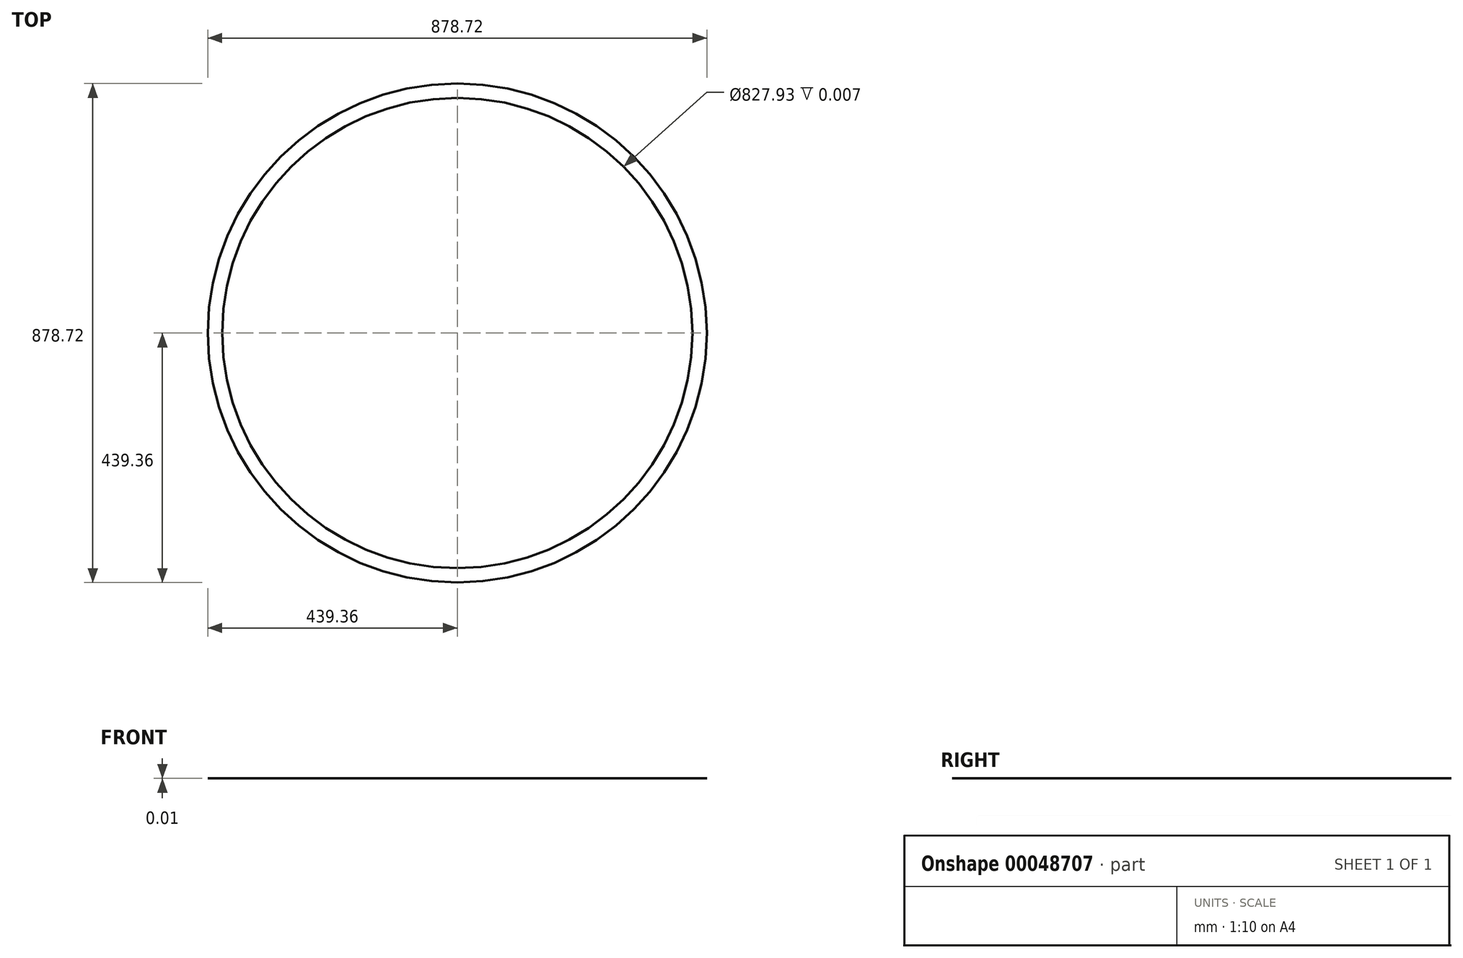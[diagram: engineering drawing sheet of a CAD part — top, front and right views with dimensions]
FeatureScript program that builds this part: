
annotation { "Feature Type Name" : "Feature", "Feature Type Description" : "" }
export const myFeature = defineFeature(function(context is Context, id is Id, definition is map)
    precondition{}
    {
        {
            var Q0;
            Q0=qCreatedBy(makeId("Top.planeOp"),FACE);
            var sketch = newSketch(context, id + "F0", { "sketchPlane" : qUnion([Q0])});
            skCircle(sketch, "E0", {"center": v(0, 0) * mm, "radius": 439.36 * mm});
            skCircle(sketch, "E1", {"center": v(0, 0) * mm, "radius": 413.96 * mm});
            skSolve(sketch);
        }
        {
            var Q0;
            Q0 = qSketchRegion(id + "F0", true);
            extrude(context, id + "F1", {"entities" : qUnion([Q0]), "depth" : 3 / 457.2 * mm});
        }
    });
